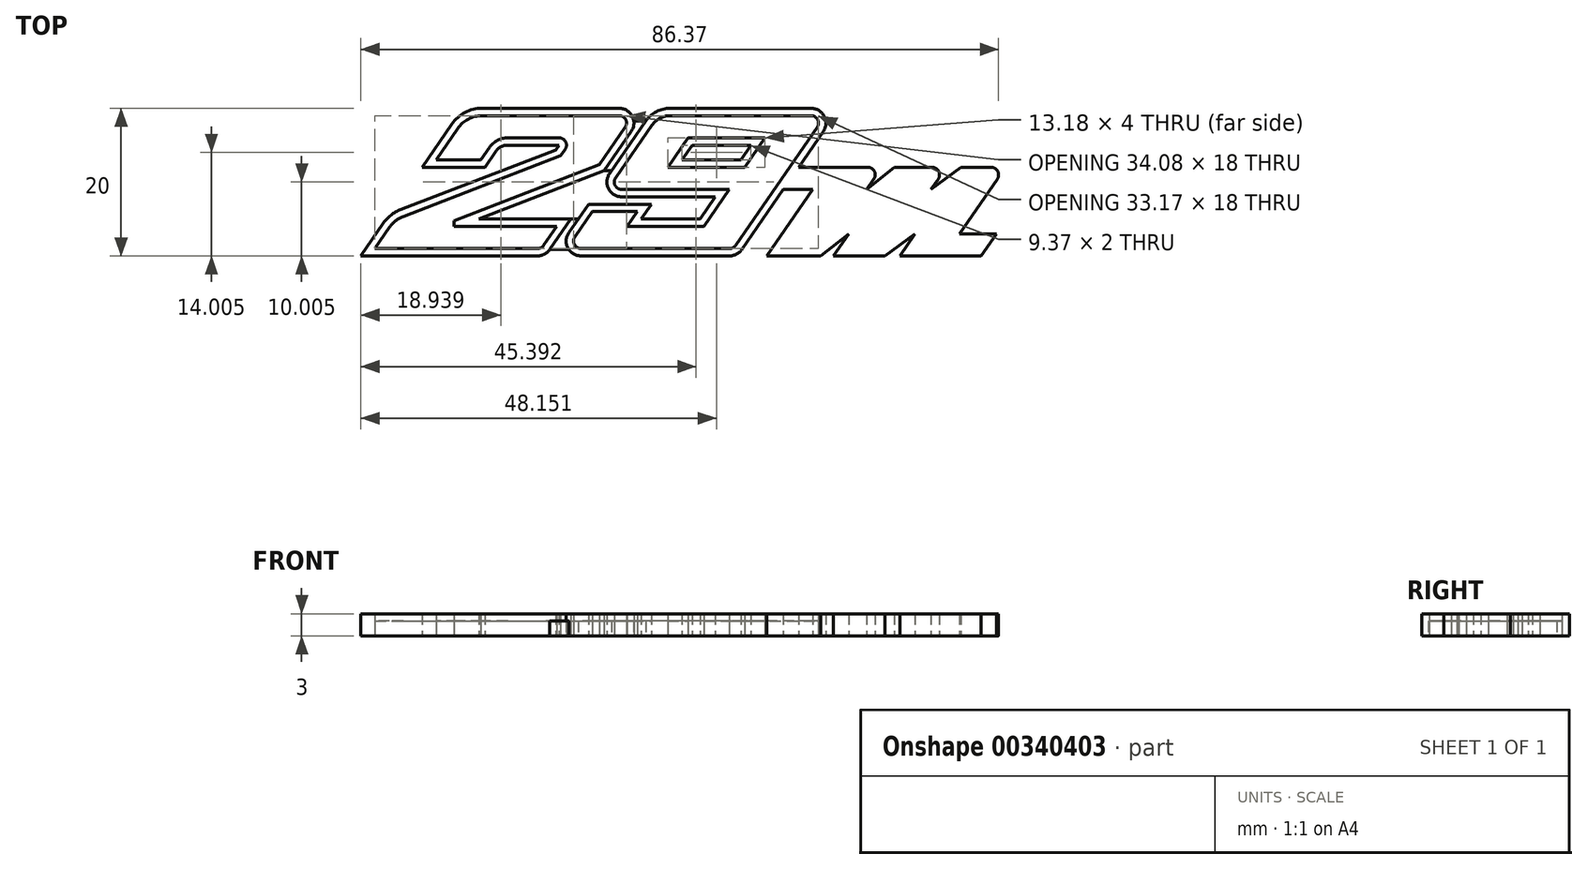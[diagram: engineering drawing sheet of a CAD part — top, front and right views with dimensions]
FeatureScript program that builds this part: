
annotation { "Feature Type Name" : "Feature", "Feature Type Description" : "" }
export const myFeature = defineFeature(function(context is Context, id is Id, definition is map)
    precondition{}
    {
        {
            var Q0;
            Q0=qCreatedBy(makeId("Top.planeOp"),FACE);
            var sketch = newSketch(context, id + "F0", { "sketchPlane" : qUnion([Q0])});
            skLineSegment(sketch, "E0", {"start": v(-25.85, -3.97) * mm, "end": v(-13.4, -3.97) * mm});
            skLineSegment(sketch, "E1", {"start": v(13.15, -8.97) * mm, "end": v(20.43, -8.97) * mm});
            skLineSegment(sketch, "E2", {"start": v(22.15, -8.97) * mm, "end": v(29.15, -8.97) * mm});
            skLineSegment(sketch, "E3", {"start": v(31.15, -8.97) * mm, "end": v(42.15, -8.97) * mm});
            skLineSegment(sketch, "E4", {"start": v(39.21, -5.97) * mm, "end": v(44.21, -5.97) * mm});
            skLineSegment(sketch, "E5", {"start": v(15.35, 0.03) * mm, "end": v(19.35, 0.03) * mm});
            skLineSegment(sketch, "E6", {"start": v(-25.44, 11.03) * mm, "end": v(-6.87, 11.03) * mm});
            skArc(sketch, "E7", {"start": v(-25.44, 11.03) * mm, "mid": v(-27.76, 10.46) * mm, "end": v(-29.55, 8.87) * mm});
            skLineSegment(sketch, "E8", {"start": v(-21.96, 6.03) * mm, "end": v(-15.01, 6.03) * mm});
            skArc(sketch, "E9", {"start": v(-21.96, 6.03) * mm, "mid": v(-22.89, 5.8) * mm, "end": v(-23.6, 5.17) * mm});
            skLineSegment(sketch, "E10", {"start": v(-33.58, 3.03) * mm, "end": v(-25.08, 3.03) * mm});
            skLineSegment(sketch, "E11", {"start": v(-29.55, 8.87) * mm, "end": v(-33.58, 3.03) * mm});
            skLineSegment(sketch, "E12", {"start": v(-38.8, -4.53) * mm, "end": v(-41.85, -8.97) * mm});
            skArc(sketch, "E13", {"start": v(-36.47, -2.7) * mm, "mid": v(-37.77, -3.44) * mm, "end": v(-38.8, -4.53) * mm});
            skLineSegment(sketch, "E14", {"start": v(-23.6, 5.17) * mm, "end": v(-25.08, 3.03) * mm});
            skLineSegment(sketch, "E15", {"start": v(-5.22, 7.9) * mm, "end": v(-8.9, 2.57) * mm});
            skLineSegment(sketch, "E16", {"start": v(-13.4, -3.97) * mm, "end": v(-16.26, -8.1) * mm});
            skArc(sketch, "E17", {"start": v(-5.22, 7.9) * mm, "mid": v(-5.1, 9.96) * mm, "end": v(-6.87, 11.03) * mm});
            skLineSegment(sketch, "E18", {"start": v(-15.01, 6.03) * mm, "end": v(-15.45, 5.4) * mm});
            skLineSegment(sketch, "E19", {"start": v(44.21, -5.97) * mm, "end": v(42.15, -8.97) * mm});
            skLineSegment(sketch, "E20", {"start": v(19.35, 0.03) * mm, "end": v(13.15, -8.97) * mm});
            skLineSegment(sketch, "E21", {"start": v(27.63, 1.47) * mm, "end": v(26.64, 0.03) * mm});
            skArc(sketch, "E22", {"start": v(27.63, 1.47) * mm, "mid": v(27.7, 2.5) * mm, "end": v(26.8, 3.03) * mm});
            skLineSegment(sketch, "E23", {"start": v(-25.85, -3.97) * mm, "end": v(-8.9, 2.57) * mm});
            skLineSegment(sketch, "E24", {"start": v(-36.47, -2.7) * mm, "end": v(-15.45, 5.4) * mm});
            skLineSegment(sketch, "E25", {"start": v(-41.85, -8.97) * mm, "end": v(-17.9, -8.97) * mm});
            skArc(sketch, "E26", {"start": v(-17.9, -8.97) * mm, "mid": v(-16.97, -8.74) * mm, "end": v(-16.26, -8.1) * mm});
            skLineSegment(sketch, "E27", {"start": v(43.52, 3.03) * mm, "end": v(39.42, 3.03) * mm});
            skLineSegment(sketch, "E28", {"start": v(35.52, 3.03) * mm, "end": v(30.42, 3.03) * mm});
            skLineSegment(sketch, "E29", {"start": v(26.8, 3.03) * mm, "end": v(17.42, 3.03) * mm});
            skLineSegment(sketch, "E30", {"start": v(13.15, -8.97) * mm, "end": v(20.15, -8.97) * mm});
            skLineSegment(sketch, "E31", {"start": v(22.15, -8.97) * mm, "end": v(25.15, -8.97) * mm});
            skLineSegment(sketch, "E32", {"start": v(25.15, 3.03) * mm, "end": v(26.8, 3.03) * mm});
            skLineSegment(sketch, "E33", {"start": v(30.42, 3.03) * mm, "end": v(35.52, 3.03) * mm});
            skLineSegment(sketch, "E34", {"start": v(39.42, 3.03) * mm, "end": v(40.15, 3.03) * mm});
            skLineSegment(sketch, "E35", {"start": v(24.21, -5.97) * mm, "end": v(22.15, -8.97) * mm});
            skLineSegment(sketch, "E36", {"start": v(36.34, 1.47) * mm, "end": v(35.35, 0.03) * mm});
            skArc(sketch, "E37", {"start": v(36.34, 1.47) * mm, "mid": v(36.4, 2.5) * mm, "end": v(35.52, 3.03) * mm});
            skLineSegment(sketch, "E38", {"start": v(33.21, -5.97) * mm, "end": v(31.15, -8.97) * mm});
            skLineSegment(sketch, "E39", {"start": v(20.43, -8.97) * mm, "end": v(24.21, -5.97) * mm});
            skLineSegment(sketch, "E40", {"start": v(29.15, -8.97) * mm, "end": v(33.21, -5.97) * mm});
            skLineSegment(sketch, "E41", {"start": v(39.42, 3.03) * mm, "end": v(35.35, 0.03) * mm});
            skLineSegment(sketch, "E42", {"start": v(30.42, 3.03) * mm, "end": v(26.64, 0.03) * mm});
            skLineSegment(sketch, "E43", {"start": v(44.34, 1.47) * mm, "end": v(39.21, -5.97) * mm});
            skArc(sketch, "E44", {"start": v(44.34, 1.47) * mm, "mid": v(44.4, 2.5) * mm, "end": v(43.52, 3.03) * mm});
            skLineSegment(sketch, "E45", {"start": v(19.13, 11.03) * mm, "end": v(0.04, 11.03) * mm});
            skArc(sketch, "E46", {"start": v(20.78, 7.9) * mm, "mid": v(20.9, 9.96) * mm, "end": v(19.13, 11.03) * mm});
            skLineSegment(sketch, "E47", {"start": v(10.99, 6.03) * mm, "end": v(3, 6.03) * mm});
            skLineSegment(sketch, "E48", {"start": v(6.16, -0.97) * mm, "end": v(-6.53, -0.97) * mm});
            skArc(sketch, "E49", {"start": v(-8.17, 2.17) * mm, "mid": v(-8.3, 0.1) * mm, "end": v(-6.53, -0.97) * mm});
            skLineSegment(sketch, "E50", {"start": v(-2.52, -1.97) * mm, "end": v(-11.03, -1.97) * mm});
            skLineSegment(sketch, "E51", {"start": v(9.6, 4.03) * mm, "end": v(1.61, 4.03) * mm});
            skLineSegment(sketch, "E52", {"start": v(8.1, -8.97) * mm, "end": v(-12.05, -8.97) * mm});
            skLineSegment(sketch, "E53", {"start": v(4.1, -3.97) * mm, "end": v(-3.9, -3.97) * mm});
            skLineSegment(sketch, "E54", {"start": v(9.74, -8.1) * mm, "end": v(20.78, 7.9) * mm});
            skArc(sketch, "E55", {"start": v(8.1, -8.97) * mm, "mid": v(9.03, -8.74) * mm, "end": v(9.74, -8.1) * mm});
            skLineSegment(sketch, "E56", {"start": v(4.1, -3.97) * mm, "end": v(6.16, -0.97) * mm});
            skLineSegment(sketch, "E57", {"start": v(9.6, 4.03) * mm, "end": v(10.99, 6.03) * mm});
            skLineSegment(sketch, "E58", {"start": v(-13.7, -5.83) * mm, "end": v(-11.03, -1.97) * mm});
            skArc(sketch, "E59", {"start": v(-13.7, -5.83) * mm, "mid": v(-13.82, -7.9) * mm, "end": v(-12.05, -8.97) * mm});
            skLineSegment(sketch, "E60", {"start": v(-8.17, 2.17) * mm, "end": v(-3.25, 9.3) * mm});
            skLineSegment(sketch, "E61", {"start": v(-3.9, -3.97) * mm, "end": v(-2.52, -1.97) * mm});
            skLineSegment(sketch, "E62", {"start": v(1.61, 4.03) * mm, "end": v(3, 6.03) * mm});
            skArc(sketch, "E63", {"start": v(0.04, 11.03) * mm, "mid": v(-1.82, 10.58) * mm, "end": v(-3.25, 9.3) * mm});
            skLineSegment(sketch, "E64", {"start": v(-39.95, -7.97) * mm, "end": v(-17.9, -7.97) * mm});
            skLineSegment(sketch, "E65", {"start": v(-37.97, -5.1) * mm, "end": v(-39.95, -7.97) * mm});
            skLineSegment(sketch, "E66", {"start": v(-36.11, -3.63) * mm, "end": v(-14.8, 4.58) * mm});
            skLineSegment(sketch, "E67", {"start": v(-21.96, 7.03) * mm, "end": v(-15.01, 7.03) * mm});
            skArc(sketch, "E68", {"start": v(-21.96, 7.03) * mm, "mid": v(-23.35, 6.7) * mm, "end": v(-24.43, 5.74) * mm});
            skLineSegment(sketch, "E69", {"start": v(-24.43, 5.74) * mm, "end": v(-25.6, 4.03) * mm});
            skLineSegment(sketch, "E70", {"start": v(-31.67, 4.03) * mm, "end": v(-25.6, 4.03) * mm});
            skLineSegment(sketch, "E71", {"start": v(-28.73, 8.3) * mm, "end": v(-31.67, 4.03) * mm});
            skArc(sketch, "E72", {"start": v(-25.44, 10.03) * mm, "mid": v(-27.3, 9.58) * mm, "end": v(-28.73, 8.3) * mm});
            skLineSegment(sketch, "E73", {"start": v(-25.44, 10.03) * mm, "end": v(-6.87, 10.03) * mm});
            skArc(sketch, "E74", {"start": v(-6.05, 8.47) * mm, "mid": v(-5.98, 9.5) * mm, "end": v(-6.87, 10.03) * mm});
            skLineSegment(sketch, "E75", {"start": v(-6.05, 8.47) * mm, "end": v(-9.55, 3.39) * mm});
            skLineSegment(sketch, "E76", {"start": v(-29.22, -4.2) * mm, "end": v(-9.55, 3.39) * mm});
            skLineSegment(sketch, "E77", {"start": v(-29.22, -4.97) * mm, "end": v(-15.31, -4.97) * mm});
            skLineSegment(sketch, "E78", {"start": v(-15.31, -4.97) * mm, "end": v(-17.08, -7.53) * mm});
            skArc(sketch, "E79", {"start": v(-17.9, -7.97) * mm, "mid": v(-17.44, -7.85) * mm, "end": v(-17.08, -7.53) * mm});
            skArc(sketch, "E80", {"start": v(-36.11, -3.63) * mm, "mid": v(-37.15, -4.22) * mm, "end": v(-37.97, -5.1) * mm});
            skLineSegment(sketch, "E81", {"start": v(-14.19, 5.47) * mm, "end": v(-14.8, 4.58) * mm});
            skArc(sketch, "E82", {"start": v(-7.35, 1.6) * mm, "mid": v(-7.41, 0.57) * mm, "end": v(-6.53, 0.03) * mm});
            skLineSegment(sketch, "E83", {"start": v(8.06, 0.03) * mm, "end": v(-6.53, 0.03) * mm});
            skLineSegment(sketch, "E84", {"start": v(-7.35, 1.6) * mm, "end": v(-2.43, 8.74) * mm});
            skArc(sketch, "E85", {"start": v(0.04, 10.03) * mm, "mid": v(-1.36, 9.7) * mm, "end": v(-2.43, 8.74) * mm});
            skLineSegment(sketch, "E86", {"start": v(19.13, 10.03) * mm, "end": v(0.04, 10.03) * mm});
            skArc(sketch, "E87", {"start": v(19.95, 8.47) * mm, "mid": v(20.02, 9.5) * mm, "end": v(19.13, 10.03) * mm});
            skLineSegment(sketch, "E88", {"start": v(8.92, -7.53) * mm, "end": v(19.95, 8.47) * mm});
            skLineSegment(sketch, "E89", {"start": v(8.1, -7.97) * mm, "end": v(-12.05, -7.97) * mm});
            skArc(sketch, "E90", {"start": v(8.1, -7.97) * mm, "mid": v(8.56, -7.85) * mm, "end": v(8.92, -7.53) * mm});
            skArc(sketch, "E91", {"start": v(-12.87, -6.4) * mm, "mid": v(-12.93, -7.43) * mm, "end": v(-12.05, -7.97) * mm});
            skLineSegment(sketch, "E92", {"start": v(-12.87, -6.4) * mm, "end": v(-10.5, -2.97) * mm});
            skLineSegment(sketch, "E93", {"start": v(-4.43, -2.97) * mm, "end": v(-10.5, -2.97) * mm});
            skLineSegment(sketch, "E94", {"start": v(-5.8, -4.97) * mm, "end": v(-4.43, -2.97) * mm});
            skLineSegment(sketch, "E95", {"start": v(4.62, -4.97) * mm, "end": v(-5.8, -4.97) * mm});
            skLineSegment(sketch, "E96", {"start": v(4.62, -4.97) * mm, "end": v(8.06, 0.03) * mm});
            skLineSegment(sketch, "E97", {"start": v(10.13, 3.03) * mm, "end": v(-0.29, 3.03) * mm});
            skLineSegment(sketch, "E98", {"start": v(-0.29, 3.03) * mm, "end": v(2.47, 7.03) * mm});
            skLineSegment(sketch, "E99", {"start": v(12.9, 7.03) * mm, "end": v(2.47, 7.03) * mm});
            skLineSegment(sketch, "E100", {"start": v(10.13, 3.03) * mm, "end": v(12.9, 7.03) * mm});
            skLineSegment(sketch, "E101", {"start": v(-29.22, -4.2) * mm, "end": v(-29.22, -4.97) * mm});
            skArc(sketch, "E102", {"start": v(-14.19, 5.47) * mm, "mid": v(-14.13, 6.5) * mm, "end": v(-15.01, 7.03) * mm});
            skLineSegment(sketch, "E103", {"start": v(-13.4, -3.97) * mm, "end": v(-12.4, -3.97) * mm});
            skLineSegment(sketch, "E104", {"start": v(-8.9, 2.57) * mm, "end": v(-7.9, 2.56) * mm});
            skLineSegment(sketch, "E105", {"start": v(-3.25, 9.3) * mm, "end": v(-4.89, 9.3) * mm});
            skLineSegment(sketch, "E106", {"start": v(-16.26, -8.1) * mm, "end": v(-13.7, -8.1) * mm});
            skSolve(sketch);
        }
        {
            var Q0;
            Q0=makeQuery(id+"F0.imprint","IMPRINT",FACE,{"disambiguationData":[TD([[makeQuery(id+"F0.imprint","IMPRINT",EDGE,{"derivedFrom":sQuery(id+"F0.wireOp",EDGE,"E64")}),1.0]])]});
            var Q1;
            Q1=makeQuery(id+"F0.imprint","IMPRINT",FACE,{"disambiguationData":[TD([[makeQuery(id+"F0.imprint","IMPRINT",EDGE,{"derivedFrom":sQuery(id+"F0.wireOp",EDGE,"E82")}),1.0]])]});
            var Q2;
            Q2=makeQuery(id+"F0.imprint","IMPRINT",FACE,{"disambiguationData":[TD([[makeQuery(id+"F0.imprint","IMPRINT",EDGE,{"derivedFrom":sQuery(id+"F0.wireOp",EDGE,"E16")}),1.0]])]});
            var Q3;
            Q3=makeQuery(id+"F0.imprint","IMPRINT",FACE,{"disambiguationData":[TD([[makeQuery(id+"F0.imprint","IMPRINT",EDGE,{"derivedFrom":sQuery(id+"F0.wireOp",EDGE,"E15")}),1.0]])]});
            extrude(context, id + "F1", {"entities" : qUnion([Q0, Q1, Q2, Q3]), "depth" : 2 * mm});
        }
        {
            var Q0;
            Q0=makeQuery(id+"F0.imprint","IMPRINT",FACE,{"disambiguationData":[TD([[makeQuery(id+"F0.imprint","IMPRINT",EDGE,{"derivedFrom":sQuery(id+"F0.wireOp",EDGE,"E0")}),-1.0]])]});
            var Q1;
            Q1=makeQuery(id+"F0.imprint","IMPRINT",FACE,{"disambiguationData":[TD([[makeQuery(id+"F0.imprint","IMPRINT",EDGE,{"derivedFrom":sQuery(id+"F0.wireOp",EDGE,"E45")}),1.0]])]});
            var Q2;
            Q2=makeQuery(id+"F0.imprint","IMPRINT",FACE,{"disambiguationData":[TD([[makeQuery(id+"F0.imprint","IMPRINT",EDGE,{"derivedFrom":sQuery(id+"F0.wireOp",EDGE,"E3")}),1.0]])]});
            var Q3;
            Q3=makeQuery(id+"F0.imprint","IMPRINT",FACE,{"disambiguationData":[TD([[makeQuery(id+"F0.imprint","IMPRINT",EDGE,{"derivedFrom":sQuery(id+"F0.wireOp",EDGE,"E47")}),-1.0]])]});
            extrude(context, id + "F2", {"entities" : qUnion([Q0, Q1, Q2, Q3]), "depth" : 3 * mm});
        }
    });
